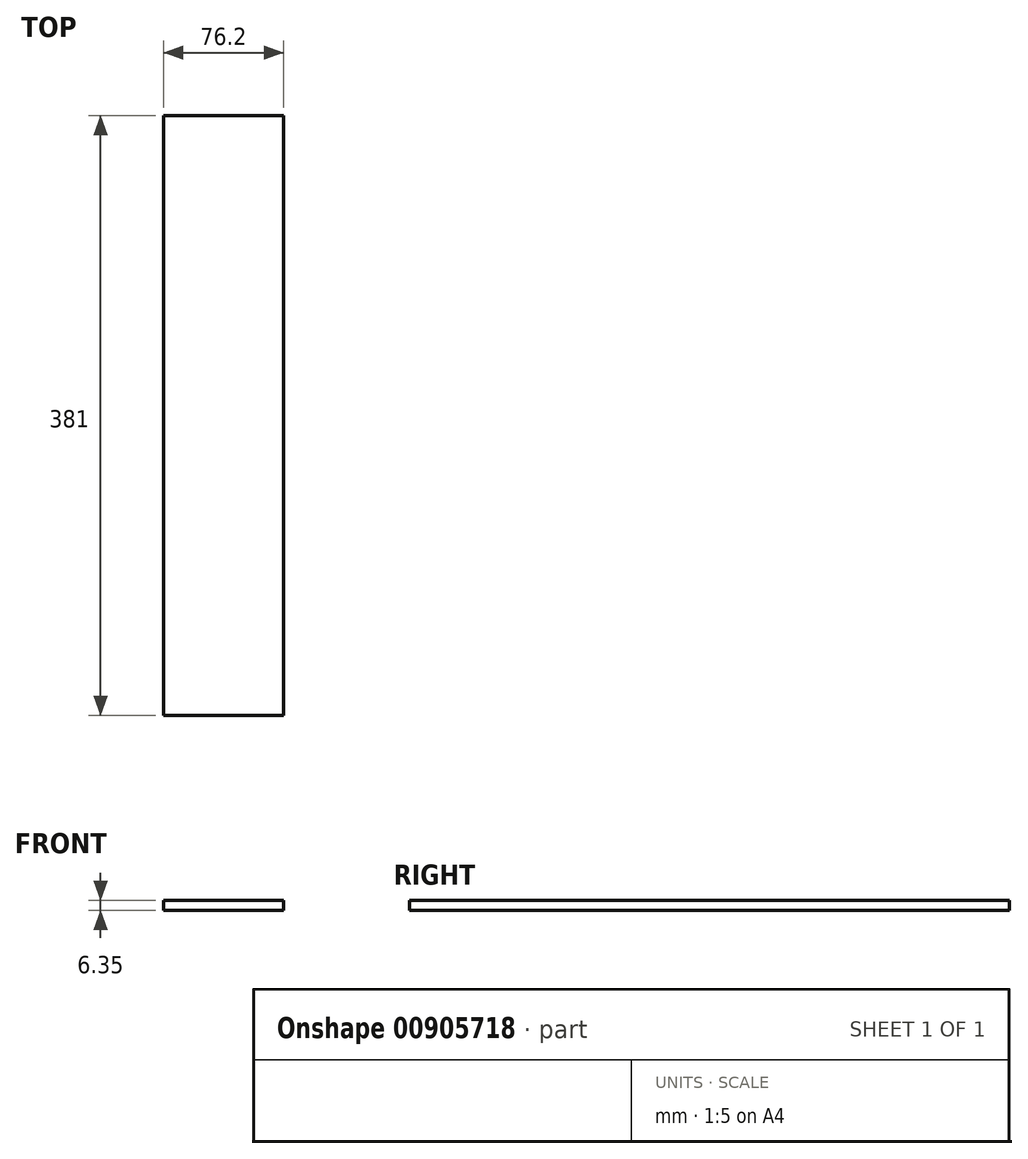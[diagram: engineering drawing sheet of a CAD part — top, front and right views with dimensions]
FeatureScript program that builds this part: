
annotation { "Feature Type Name" : "Feature", "Feature Type Description" : "" }
export const myFeature = defineFeature(function(context is Context, id is Id, definition is map)
    precondition{}
    {
        {
            var Q0;
            Q0=qCreatedBy(makeId("Right.planeOp"),FACE);
            var sketch = newSketch(context, id + "F0", { "sketchPlane" : qUnion([Q0])});
            skLineSegment(sketch, "E0.bottom", {"start": v(-4.76, 1.1) * mm, "end": v(376.24, 1.1) * mm});
            skLineSegment(sketch, "E0.top", {"start": v(-4.76, -5.25) * mm, "end": v(376.24, -5.25) * mm});
            skLineSegment(sketch, "E0.left", {"start": v(-4.76, 1.1) * mm, "end": v(-4.76, -5.25) * mm});
            skLineSegment(sketch, "E0.right", {"start": v(376.24, 1.1) * mm, "end": v(376.24, -5.25) * mm});
            skSolve(sketch);
        }
        {
            var Q0;
            Q0=makeQuery(id+"F0.imprint","IMPRINT",FACE,{"disambiguationData":[TD([[makeQuery(id+"F0.imprint","IMPRINT",EDGE,{"derivedFrom":sQuery(id+"F0.wireOp",EDGE,"E0.bottom")}),-1.0]])]});
            extrude(context, id + "F1", {"entities" : qUnion([Q0]), "depth" : 76.2 * mm, "offsetDistance" : 25.4 * mm});
        }
    });
